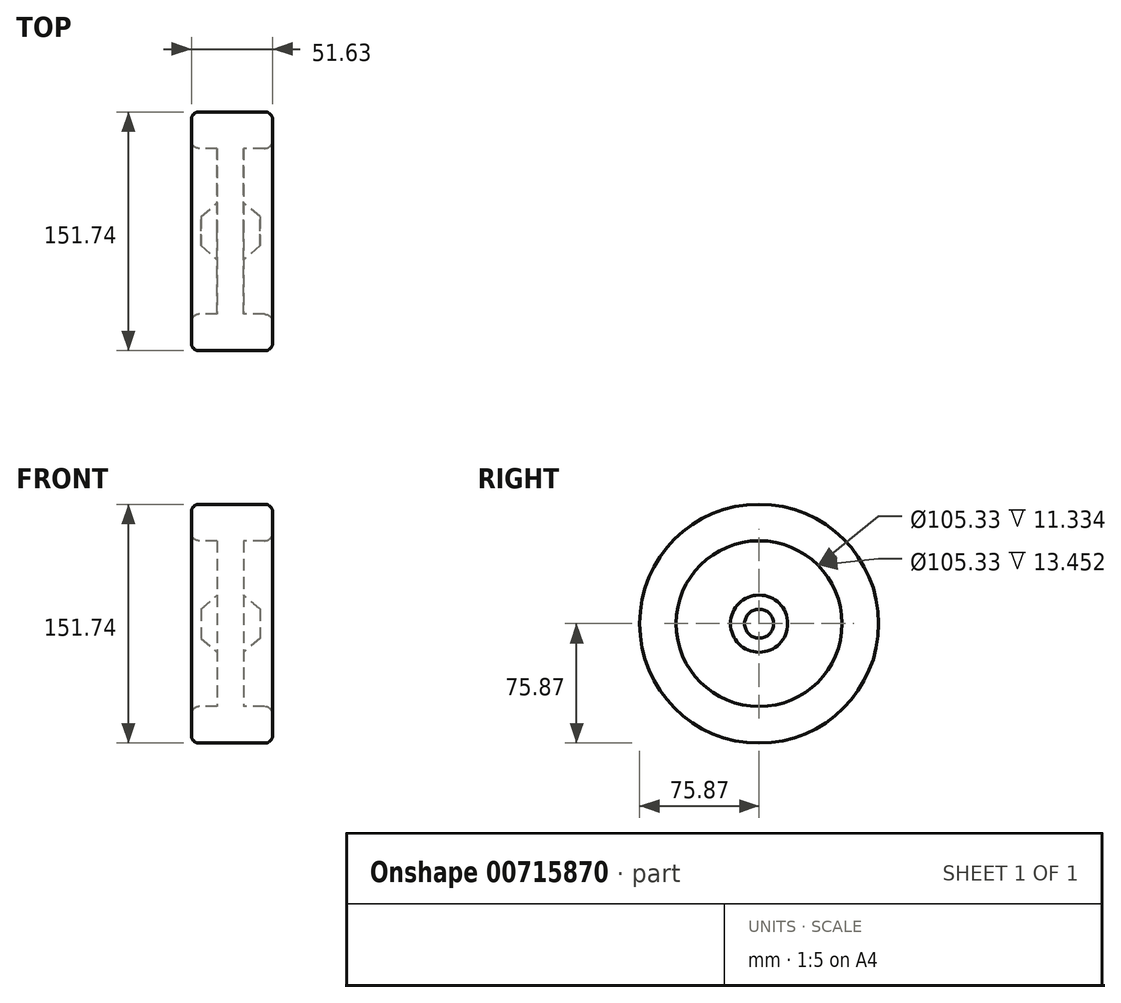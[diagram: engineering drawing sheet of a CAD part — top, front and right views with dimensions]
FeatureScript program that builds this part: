
annotation { "Feature Type Name" : "Feature", "Feature Type Description" : "" }
export const myFeature = defineFeature(function(context is Context, id is Id, definition is map)
    precondition{}
    {
        {
            var Q0;
            Q0=qCreatedBy(makeId("Front.planeOp"),FACE);
            var sketch = newSketch(context, id + "F0", { "sketchPlane" : qUnion([Q0])});
            skLineSegment(sketch, "E0.bottom", {"start": v(-24.52, 75.87) * mm, "end": v(27.11, 75.87) * mm});
            skLineSegment(sketch, "E0.top", {"start": v(-24.52, 52.67) * mm, "end": v(27.11, 52.67) * mm});
            skLineSegment(sketch, "E0.left", {"start": v(-24.52, 75.87) * mm, "end": v(-24.52, 52.67) * mm});
            skLineSegment(sketch, "E0.right", {"start": v(27.11, 75.87) * mm, "end": v(27.11, 52.67) * mm});
            skLineSegment(sketch, "E1.bottom", {"start": v(-8.1, 52.67) * mm, "end": v(8.58, 52.67) * mm});
            skLineSegment(sketch, "E1.top", {"start": v(-8.1, 0) * mm, "end": v(8.58, 0) * mm});
            skLineSegment(sketch, "E1.left", {"start": v(-8.1, 52.67) * mm, "end": v(-8.1, 0) * mm});
            skLineSegment(sketch, "E1.right", {"start": v(8.58, 52.67) * mm, "end": v(8.58, 0) * mm});
            skLineSegment(sketch, "E2", {"start": v(-8.1, 18.15) * mm, "end": v(-18.27, 9.21) * mm});
            skLineSegment(sketch, "E3", {"start": v(-18.27, 9.21) * mm, "end": v(-18.27, 0) * mm});
            skLineSegment(sketch, "E4", {"start": v(-18.27, 0) * mm, "end": v(-8.1, 0) * mm});
            skLineSegment(sketch, "E5", {"start": v(8.58, 0) * mm, "end": v(19.1, 0) * mm});
            skLineSegment(sketch, "E6", {"start": v(19.1, 0) * mm, "end": v(19.1, 9.21) * mm});
            skLineSegment(sketch, "E7", {"start": v(19.1, 9.21) * mm, "end": v(8.58, 18.15) * mm});
            skPoint(sketch, "E7.endSnap0", {"position": v(8.58, 26.33) * mm});
            skSolve(sketch);
        }
        {
            var Q0;
            Q0 = qSketchRegion(id + "F0", true);
            var Q1;
            Q1=sQuery(id+"F0.wireOp",EDGE,"E1.top");
            revolve(context, id + "F1", {"surfaceOperationType" : NewSurfaceOperationType.NEW, "entities" : qUnion([Q0]), "axis" : qUnion([Q1]), "revolveType" : RevolveType.FULL});
        }
        {
            var Q0;
            Q0=makeQuery(id+"F1.opRevolve","SWEPT_FACE",FACE,{"disambiguationData":[OSD([sQuery(id+"F0.wireOp",EDGE,"E0.left")])]});
            var Q1;
            Q1=makeQuery(id+"F1.opRevolve","SWEPT_EDGE",EDGE,{"disambiguationData":[OSD([sQuery(id+"F0.wireOp",EDGE,"E0.bottom"),sQuery(id+"F0.wireOp",EDGE,"E0.right")])]});
            var Q2;
            Q2=makeQuery(id+"F1.opRevolve","SWEPT_EDGE",EDGE,{"disambiguationData":[OSD([sQuery(id+"F0.wireOp",EDGE,"E0.top"),sQuery(id+"F0.wireOp",EDGE,"E0.right")])]});
            fillet(context, id + "F2", {"entities" : qUnion([Q0, Q1, Q2]), "radius" : 5.08 * mm, "tangentPropagation" : true, "allowEdgeOverflow" : false});
        }
    });
